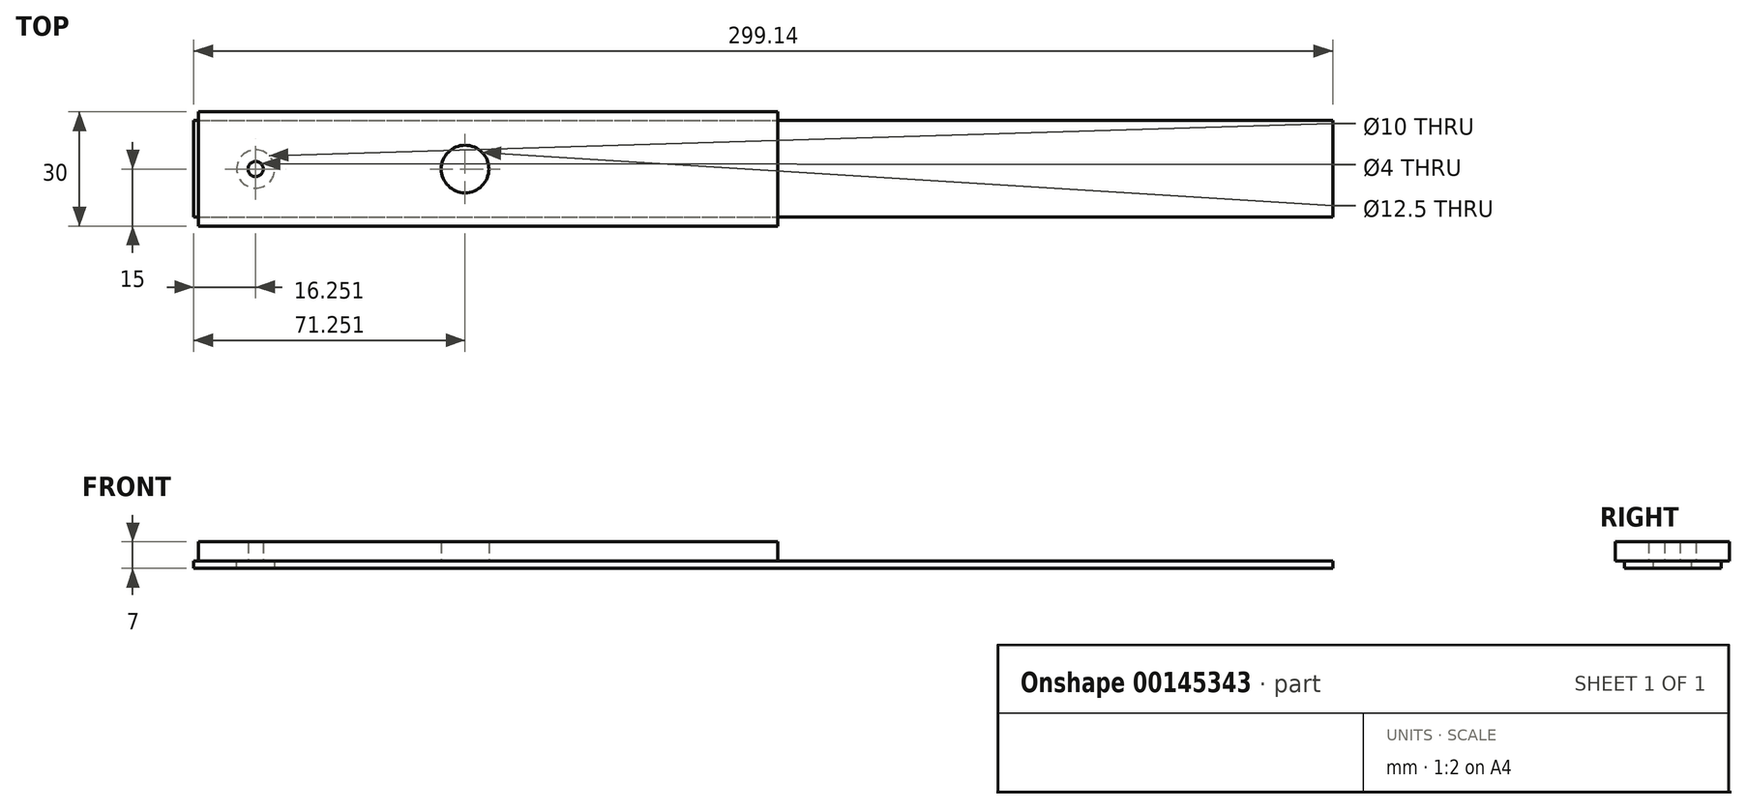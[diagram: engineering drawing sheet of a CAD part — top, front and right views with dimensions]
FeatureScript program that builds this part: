
annotation { "Feature Type Name" : "Feature", "Feature Type Description" : "" }
export const myFeature = defineFeature(function(context is Context, id is Id, definition is map)
    precondition{}
    {
        {
            var Q0;
            Q0=qCreatedBy(makeId("Top.planeOp"),FACE);
            var sketch = newSketch(context, id + "F0", { "sketchPlane" : qUnion([Q0])});
            skLineSegment(sketch, "E0.bottom", {"start": v(-33.86, 15) * mm, "end": v(118.3, 15) * mm});
            skLineSegment(sketch, "E0.top", {"start": v(-33.86, -15) * mm, "end": v(118.3, -15) * mm});
            skLineSegment(sketch, "E0.left", {"start": v(-33.86, 15) * mm, "end": v(-33.86, -15) * mm});
            skLineSegment(sketch, "E0.right", {"start": v(118.3, 15) * mm, "end": v(118.3, -15) * mm});
            skCircle(sketch, "E1", {"center": v(-18.86, 0) * mm, "radius": 2 * mm});
            skCircle(sketch, "E2", {"center": v(36.14, 0) * mm, "radius": 6.25 * mm});
            skLineSegment(sketch, "E3", {"start": v(36.14, 0) * mm, "end": v(-18.86, 0) * mm, "construction": true});
            skSolve(sketch);
        }
        {
            var Q0;
            Q0 = qSketchRegion(id + "F0", true);
            extrude(context, id + "F1", {"entities" : qUnion([Q0]), "depth" : 5 * mm});
        }
        {
            var Q0;
            Q0=qCreatedBy(makeId("Top.planeOp"),FACE);
            var Q1;
            Q1=makeQuery(id+"F1.opExtrude","CAP_FACE",FACE,{"disambiguationData":[OSD([sQuery(id+"F0.wireOp",EDGE,"E0.bottom"),sQuery(id+"F0.wireOp",EDGE,"E0.top"),sQuery(id+"F0.wireOp",EDGE,"E0.left"),sQuery(id+"F0.wireOp",EDGE,"E0.right"),sQuery(id+"F0.wireOp",EDGE,"E1"),sQuery(id+"F0.wireOp",EDGE,"E2")])],"isStart":false});
            var sketch = newSketch(context, id + "F2", { "sketchPlane" : qUnion([Q0, Q1])});
            skCircle(sketch, "E4", {"center": v(-18.86, 0) * mm, "radius": 5 * mm});
            skLineSegment(sketch, "E5.bottom", {"start": v(-35.11, 12.8) * mm, "end": v(264.03, 12.8) * mm});
            skLineSegment(sketch, "E5.top", {"start": v(-35.11, -12.58) * mm, "end": v(264.03, -12.58) * mm});
            skLineSegment(sketch, "E5.left", {"start": v(-35.11, 12.8) * mm, "end": v(-35.11, -12.58) * mm});
            skLineSegment(sketch, "E5.right", {"start": v(264.03, 12.8) * mm, "end": v(264.03, -12.58) * mm});
            skSolve(sketch);
        }
        {
            var Q0;
            Q0 = qSketchRegion(id + "F2", true);
            extrude(context, id + "F3", {"entities" : qUnion([Q0]), "oppositeDirection" : true, "depth" : 2 * mm});
        }
    });
